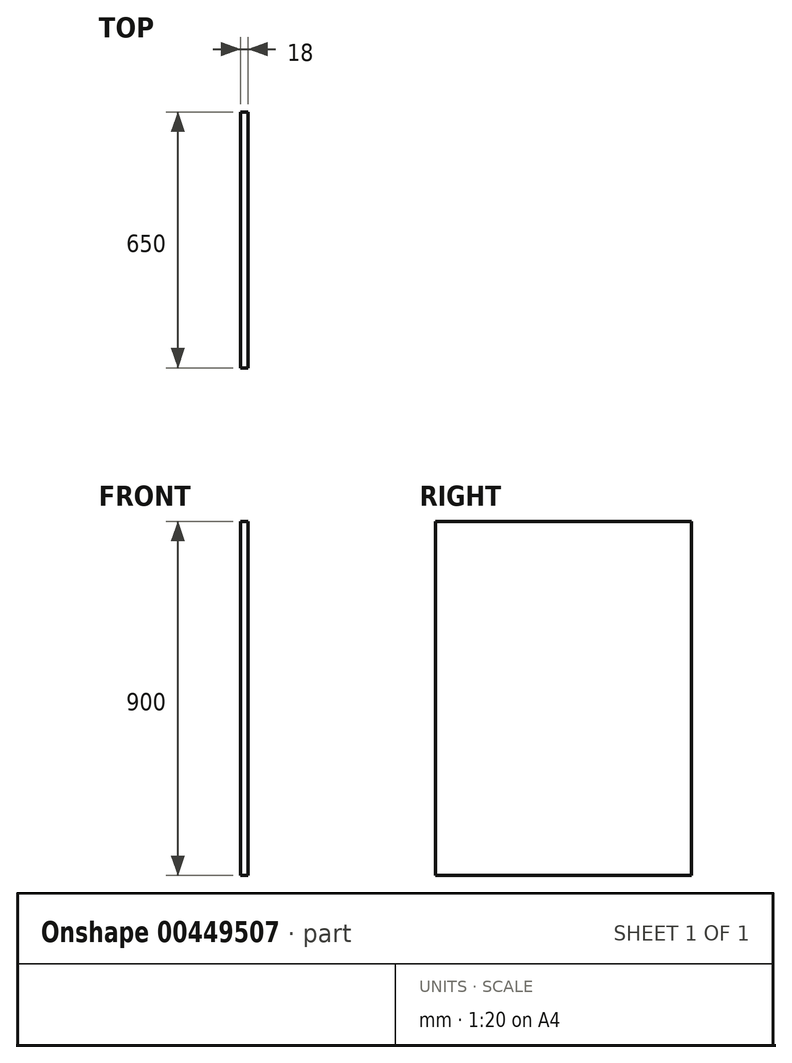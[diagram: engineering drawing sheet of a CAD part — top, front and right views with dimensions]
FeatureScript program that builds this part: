
annotation { "Feature Type Name" : "Feature", "Feature Type Description" : "" }
export const myFeature = defineFeature(function(context is Context, id is Id, definition is map)
    precondition{}
    {
        {
            var Q0;
            Q0=qCreatedBy(makeId("Right.planeOp"),FACE);
            var sketch = newSketch(context, id + "F0", { "sketchPlane" : qUnion([Q0])});
            skLineSegment(sketch, "E0.bottom", {"start": v(0, 900) * mm, "end": v(650, 900) * mm});
            skLineSegment(sketch, "E0.top", {"start": v(0, 0) * mm, "end": v(650, 0) * mm});
            skLineSegment(sketch, "E0.left", {"start": v(0, 900) * mm, "end": v(0, 0) * mm});
            skLineSegment(sketch, "E0.right", {"start": v(650, 900) * mm, "end": v(650, 0) * mm});
            skSolve(sketch);
        }
        {
            var Q0;
            Q0=qSketchRegion(id+"F0",true);
            extrude(context, id + "F1", {"entities" : qUnion([Q0]), "oppositeDirection" : true, "depth" : 18 * mm});
        }
    });
